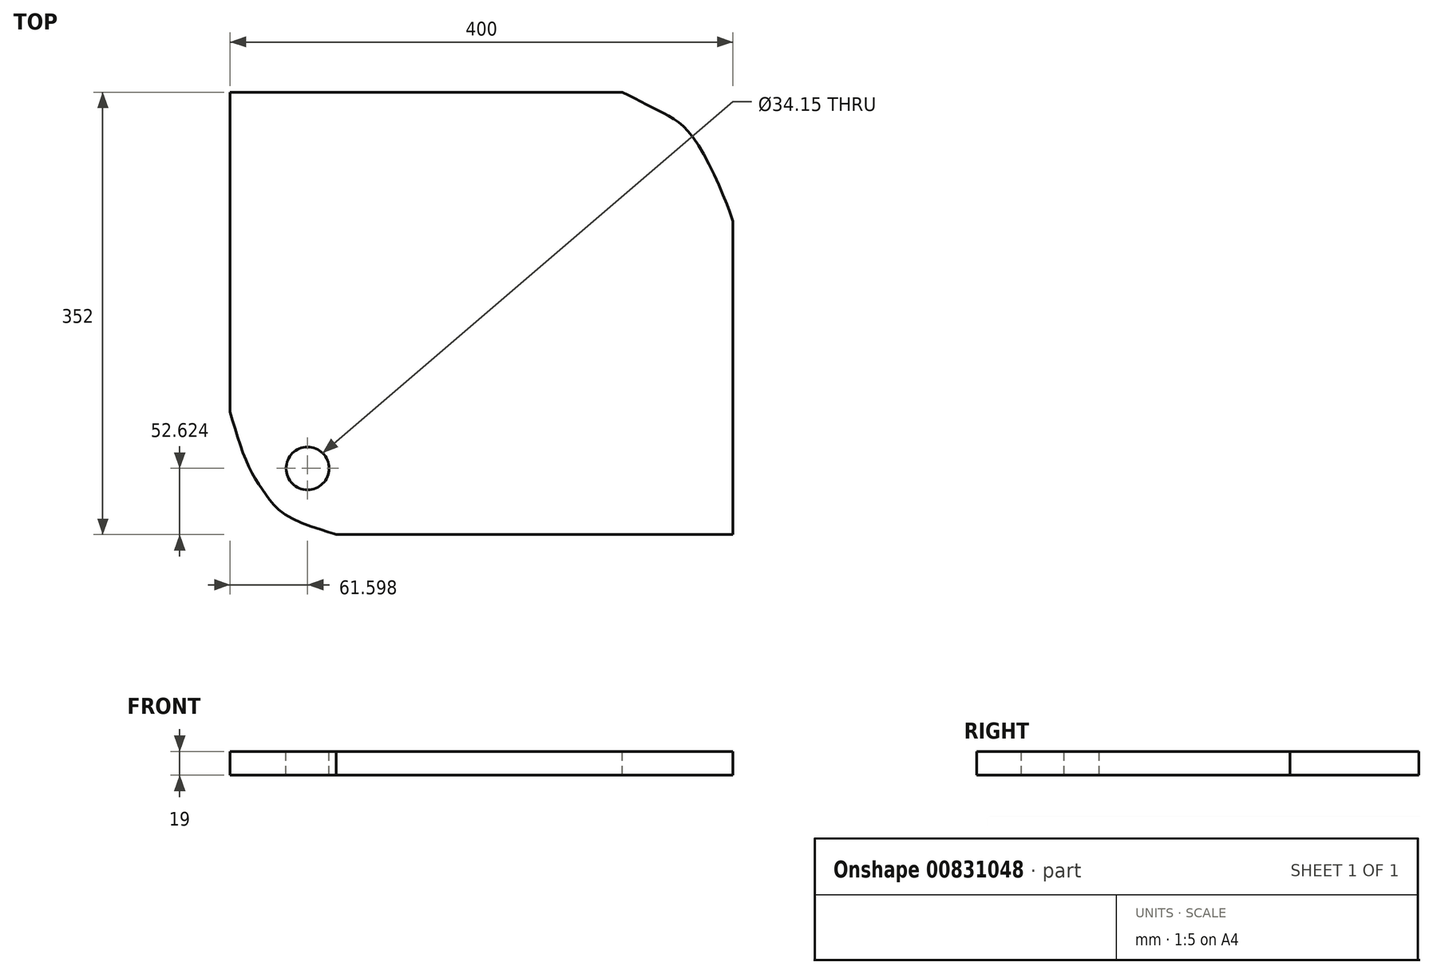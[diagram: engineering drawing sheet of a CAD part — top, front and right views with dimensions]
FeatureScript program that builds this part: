
annotation { "Feature Type Name" : "Feature", "Feature Type Description" : "" }
export const myFeature = defineFeature(function(context is Context, id is Id, definition is map)
    precondition{}
    {
        {
            var Q0;
            Q0=qCreatedBy(makeId("Top.planeOp"),FACE);
            var sketch = newSketch(context, id + "F0", { "sketchPlane" : qUnion([Q0])});
            skLineSegment(sketch, "E0.bottom", {"start": v(-200, 176) * mm, "end": v(200, 176) * mm});
            skLineSegment(sketch, "E0.top", {"start": v(-200, -176) * mm, "end": v(200, -176) * mm});
            skLineSegment(sketch, "E0.left", {"start": v(-200, 176) * mm, "end": v(-200, -176) * mm});
            skLineSegment(sketch, "E0.right", {"start": v(200, 176) * mm, "end": v(200, -176) * mm});
            skPoint(sketch, "E0.middle", {"position": v(0, 0) * mm});
            skSolve(sketch);
        }
        {
            var Q0;
            Q0=makeQuery(id+"F0.imprint","IMPRINT",FACE,{"disambiguationData":[TD([[makeQuery(id+"F0.imprint","IMPRINT",EDGE,{"derivedFrom":sQuery(id+"F0.wireOp",EDGE,"E0.bottom")}),-1.0]])]});
            extrude(context, id + "F1", {"entities" : qUnion([Q0]), "depth" : 19 * mm, "offsetDistance" : 25 * mm});
        }
        {
            var Q0;
            Q0=makeQuery(id+"F1.opExtrude","CAP_FACE",FACE,{"disambiguationData":[OSD([sQuery(id+"F0.wireOp",EDGE,"E0.bottom"),sQuery(id+"F0.wireOp",EDGE,"E0.top"),sQuery(id+"F0.wireOp",EDGE,"E0.left"),sQuery(id+"F0.wireOp",EDGE,"E0.right")])],"isStart":false});
            var sketch = newSketch(context, id + "F2", { "sketchPlane" : qUnion([Q0])});
            skFitSpline(sketch, "E1", {"points": [v(-200, -78.36) * mm, v(-186.45, -119.07) * mm, v(-172.9, -142.53) * mm, v(-150.13, -163.5) * mm, v(-115.63, -176) * mm, v(-117.48, -176) * mm], "startDerivative": vector(47.8, -165.26) * mm, "endDerivative": vector(-52.54, 4.13) * mm});
            skFitSpline(sketch, "E2", {"points": [v(111.97, 176) * mm, v(143.8, 159.76) * mm, v(170.56, 136.81) * mm, v(200, 73.26) * mm, v(200, 71.89) * mm], "startDerivative": vector(119.7, -60.64) * mm, "endDerivative": vector(-5, -13.75) * mm});
            skSolve(sketch);
        }
        {
            var Q0;
            {var subQ0=sQuery(id+"F2.wireOp",EDGE,"E1");var subQ1=makeQuery(id+"F1.opExtrude","CAP_EDGE",EDGE,{"disambiguationData":[OSD([sQuery(id+"F0.wireOp",EDGE,"E0.left")])],"isStart":false});var subQ2=makeQuery(id+"F2.imprint","INTERSECT",VERTEX,{"derivedFrom":[subQ1,subQ0]});Q0=makeQuery(id+"F2.imprint","IMPRINT",FACE,{"disambiguationData":[TD([[makeQuery(id+"F2.imprint","IMPRINT",EDGE,{"disambiguationData":[TD([[subQ2,-1.0]])],"derivedFrom":subQ0}),-1.0]])]});}
            var Q1;
            {var subQ0=sQuery(id+"F2.wireOp",EDGE,"E2");var subQ1=makeQuery(id+"F1.opExtrude","CAP_EDGE",EDGE,{"disambiguationData":[OSD([sQuery(id+"F0.wireOp",EDGE,"E0.bottom")])],"isStart":false});var subQ2=makeQuery(id+"F2.imprint","INTERSECT",VERTEX,{"derivedFrom":[subQ1,subQ0]});Q1=makeQuery(id+"F2.imprint","IMPRINT",FACE,{"disambiguationData":[TD([[makeQuery(id+"F2.imprint","IMPRINT",EDGE,{"disambiguationData":[TD([[subQ2,-1.0]])],"derivedFrom":subQ0}),1.0]])]});}
            extrude(context, id + "F3", {"entities" : qUnion([Q0, Q1]), "operationType" : NewBodyOperationType.REMOVE, "endBound" : BoundingType.THROUGH_ALL, "oppositeDirection" : true, "depth" : 25 * mm, "offsetDistance" : 25 * mm});
        }
        {
            var Q0;
            Q0=makeQuery(id+"F1.opExtrude","CAP_FACE",FACE,{"disambiguationData":[OSD([sQuery(id+"F0.wireOp",EDGE,"E0.bottom"),sQuery(id+"F0.wireOp",EDGE,"E0.top"),sQuery(id+"F0.wireOp",EDGE,"E0.left"),sQuery(id+"F0.wireOp",EDGE,"E0.right")])],"isStart":false});
            var sketch = newSketch(context, id + "F4", { "sketchPlane" : qUnion([Q0])});
            skCircle(sketch, "E3", {"center": v(-138.4, -123.38) * mm, "radius": 17.08 * mm});
            skSolve(sketch);
        }
        {
            var Q0;
            Q0=makeQuery(id+"F4.imprint","IMPRINT",FACE,{"disambiguationData":[TD([[makeQuery(id+"F4.imprint","IMPRINT",EDGE,{"derivedFrom":sQuery(id+"F4.wireOp",EDGE,"E3")}),1.0]])]});
            extrude(context, id + "F5", {"entities" : qUnion([Q0]), "operationType" : NewBodyOperationType.REMOVE, "endBound" : BoundingType.THROUGH_ALL, "oppositeDirection" : true, "depth" : 25 * mm, "offsetDistance" : 25 * mm});
        }
    });
